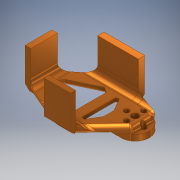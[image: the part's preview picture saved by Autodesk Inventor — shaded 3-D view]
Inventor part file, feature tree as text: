
AUTODESK INVENTOR PART (.ipt)
format: ipt  version: 2017 SP1 (Build 210196100, 196)  size: 385,024 bytes
history: native  units: mm
features: extrude x5, sketch x5, chamfer x3, fillet x3
ambient origin geometry x8: Origin, YZ Plane, XZ Plane, XY Plane, X Axis, Y Axis, Z Axis, Center Point
bodies: Body1 (feature_tree)
feature tree (16):
  extrude  "Extrusion3"  Depth=4.2mm TaperAngle=0.0deg
  extrude  "Extrusion4"  Depth=41.0mm
  extrude  "Extrusion5"  Depth=23.0mm TaperAngle=0.0deg
  extrude  "Extrusion6"  Depth=23.0mm TaperAngle=0.0deg
  extrude  "Extrusion7"  Depth=4.2mm TaperAngle=45.0deg
  chamfer  "Chamfer1"  Distance=3.0mm
  chamfer  "Chamfer2"  Distance=4.0mm
  fillet  "Fillet1"  Radius=5.0mm
  fillet  "Fillet2"  Radius=3.0mm
  fillet  "Fillet3"  [1 undecoded]
  chamfer  "Chamfer3"  [1 undecoded]
  sketch  "Sketch3"  dims[d12=3.6mm d13=4.2mm d14=0.0mm]
  sketch  "Sketch4"  dims[d16=60.6mm d17=41.0mm]
  sketch  "Sketch5"  dims[d18=4.2mm d19=0.0mm d20=23.0mm d21=3.25mm d22=0.0mm d23=0.0mm]
  sketch  "Sketch6"  dims[d24=23.0mm d25=0.0mm d26=23.0mm d27=0.0mm]
  sketch  "Sketch7"  dims[d28=4.2mm d29=2.0mm d30=45.0deg d31=4.2mm d32=2.0mm d33=45.0deg d34=3.0mm d35=4.0mm d36=5.0mm d37=3.0mm d38=2.0mm d39=45.0deg]
note: 2 required parameter values undecoded (feature->parameter linkage not recoverable at this tier; creation-order binding heuristic only, values carry confidence <= 0.55)
